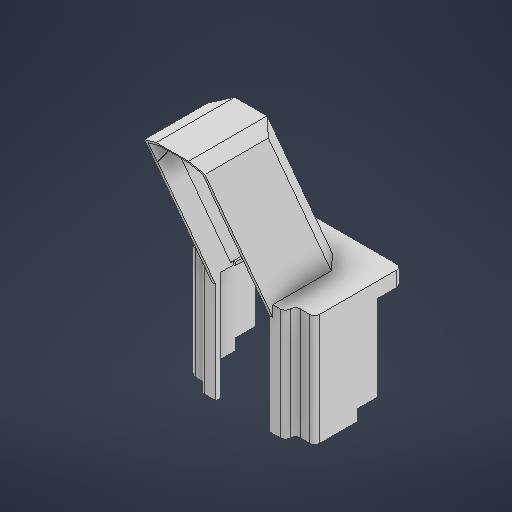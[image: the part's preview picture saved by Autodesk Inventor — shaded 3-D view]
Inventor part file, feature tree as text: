
AUTODESK INVENTOR PART (.ipt)
format: ipt  version: 2025 (Build 290162000, 162)  size: 446,976 bytes
history: native  units: in
note: dims shown in document units (in); Inventor stores cm internally (conversion verified against a paired STEP export)
features: extrude x9, sketch x8, chamfer x2, plane x2, fillet x1
ambient origin geometry x8: Origin, YZ Plane, XZ Plane, XY Plane, X Axis, Y Axis, Z Axis, Center Point
bodies: Solid1 (feature_tree)
feature tree (22):
  extrude  "Extrusion1"  Depth=0.1181in
  extrude  "Extrusion2"  Depth=0.0787in
  extrude  "Extrusion3"  Depth=1.9685in
  fillet  "Fillet1"  Radius=0.9843in
  chamfer  "Chamfer1"  Distance=0.4724in
  plane  "Work Plane1"
  extrude  "Extrusion4"  Depth=0.2165in
  chamfer  "Chamfer3"  Distance=0.1181in
  extrude  "Extrusion8"  Depth=0.1969in
  extrude  "Extrusion9"  Depth=0.1378in TaperAngle=45.0deg
  plane  "Work Plane5"
  sketch  "Sketch13"  dims[d19=0.1969in d20=0.2165in]
  extrude  "Extrusion13"  Depth=0.0787in
  extrude  "Extrusion14"  Depth=0.0787in
  extrude  "Extrusion15"  Depth=1.9685in
  sketch  "Sketch1"  dims[d1=2.9577in d2=0.1181in]
  sketch  "Sketch2"  dims[d4=0.1181in d5=0.0in d6=0.0787in]
  sketch  "Sketch3"  dims[d8=4.2323in d9=0.0in d10=1.9685in d11=0.9843in]
  sketch  "Sketch4"  dims[d12=0.9449in]
  sketch  "Sketch9"  dims[d13=0.2165in]
  sketch  "Sketch10"  dims[d15=90.0deg d17=0.4724in d18=0.0in]
  sketch  "Sketch14"  dims[d22=0.1181in d23=0.1181in d27=0.1969in d28=0.1378in d29=0.0787in d30=45.0deg d31=0.0787in d32=0.0787in d33=1.9685in d34=0.5906in d36=2.126in d38=0.1575in d39=2.2835in d40=0.1378in d41=2.3622in d42=5.315in d43=2.1969in d44=0.0in d45=0.0in d47=0.1575in d53=0.5512in d54=0.0787in d55=45.0deg d57=0.1181in d65=0.315in d67=0.3937in d69=0.6201in d70=0.3937in d71=0.7579in d72=0.315in d73=0.1598in d76=0.0787in d77=0.0787in d78=0.7579in d79=0.7579in d80=0.9843in d85=0.6201in d86=0.7579in d90=3.7598in d91=0.0in d92=1.9685in d93=0.7874in d94=0.4331in d95=0.0in d117=1.378in d118=0.3937in d119=0.0in d120=0.3937in d121=0.0in d122=0.3937in d123=0.0in]
